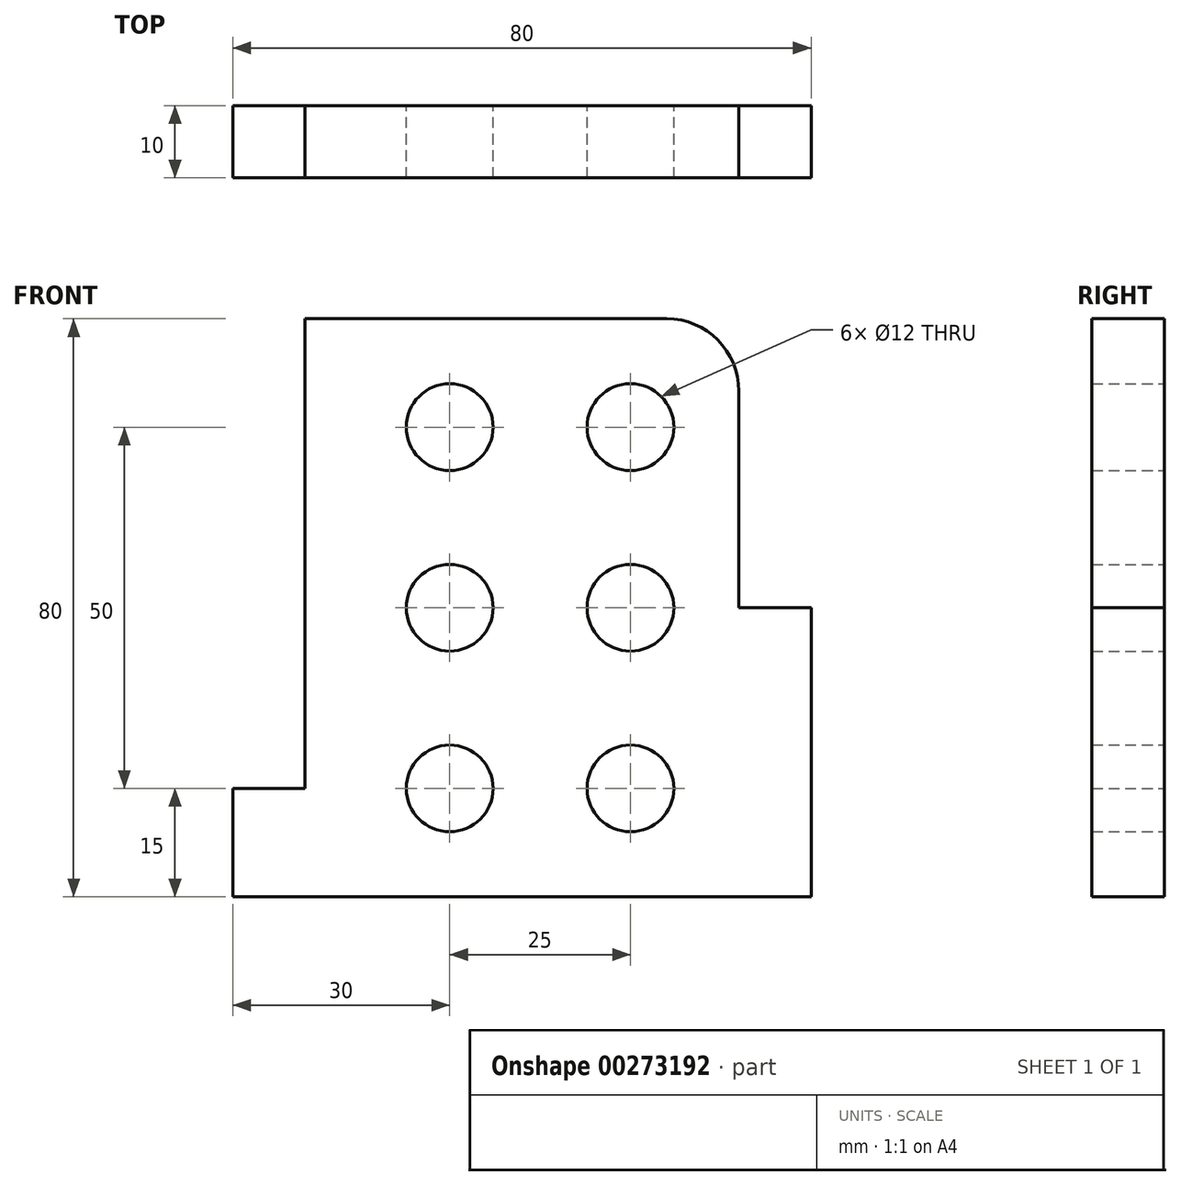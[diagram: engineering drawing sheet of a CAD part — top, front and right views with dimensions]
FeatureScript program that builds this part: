
annotation { "Feature Type Name" : "Feature", "Feature Type Description" : "" }
export const myFeature = defineFeature(function(context is Context, id is Id, definition is map)
    precondition{}
    {
        {
            var Q0;
            Q0=qCreatedBy(makeId("Front.planeOp"),FACE);
            var sketch = newSketch(context, id + "F0", { "sketchPlane" : qUnion([Q0])});
            skLineSegment(sketch, "E0", {"start": v(0, 0) * mm, "end": v(80, 0) * mm});
            skLineSegment(sketch, "E1", {"start": v(0, 0) * mm, "end": v(0, 15) * mm});
            skCircle(sketch, "E2", {"center": v(30, 15) * mm, "radius": 6 * mm});
            skCircle(sketch, "E3", {"center": v(55, 15) * mm, "radius": 6 * mm});
            skCircle(sketch, "E4", {"center": v(55, 40) * mm, "radius": 6 * mm});
            skCircle(sketch, "E5", {"center": v(30, 40) * mm, "radius": 6 * mm});
            skCircle(sketch, "E6", {"center": v(30, 65) * mm, "radius": 6 * mm});
            skCircle(sketch, "E7", {"center": v(55, 65) * mm, "radius": 6 * mm});
            skLineSegment(sketch, "E8", {"start": v(0, 15) * mm, "end": v(10, 15) * mm});
            skLineSegment(sketch, "E9", {"start": v(80, 0) * mm, "end": v(80, 40) * mm});
            skLineSegment(sketch, "E10", {"start": v(80, 40) * mm, "end": v(70, 40) * mm});
            skLineSegment(sketch, "E11", {"start": v(70, 40) * mm, "end": v(70, 70) * mm});
            skLineSegment(sketch, "E12", {"start": v(10, 15) * mm, "end": v(10, 80) * mm});
            skLineSegment(sketch, "E13", {"start": v(10, 80) * mm, "end": v(60, 80) * mm});
            skArc(sketch, "E14", {"start": v(70, 70) * mm, "mid": v(67.07, 77.07) * mm, "end": v(60, 80) * mm});
            skSolve(sketch);
        }
        {
            var Q0;
            Q0=makeQuery(id+"F0.imprint","IMPRINT",FACE,{"disambiguationData":[TD([[makeQuery(id+"F0.imprint","IMPRINT",EDGE,{"derivedFrom":sQuery(id+"F0.wireOp",EDGE,"E0")}),1.0]])]});
            extrude(context, id + "F1", {"entities" : qUnion([Q0]), "depth" : 10 * mm});
        }
    });
